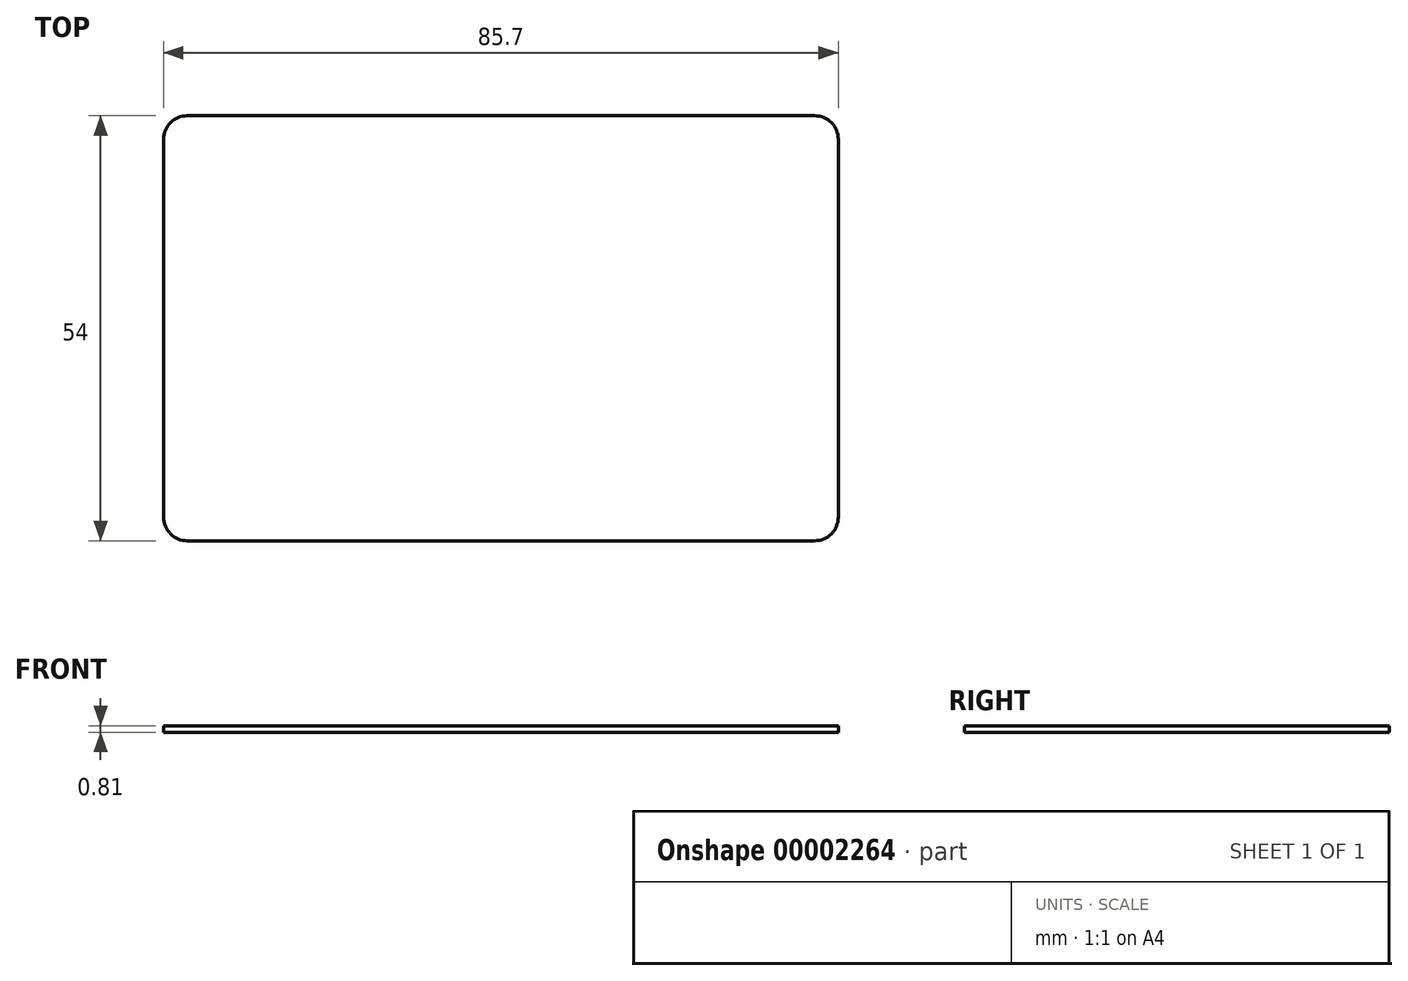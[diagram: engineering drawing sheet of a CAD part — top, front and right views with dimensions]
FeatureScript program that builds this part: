
annotation { "Feature Type Name" : "Feature", "Feature Type Description" : "" }
export const myFeature = defineFeature(function(context is Context, id is Id, definition is map)
    precondition{}
    {
        {
            var Q0;
            Q0=qCreatedBy(makeId("Top.planeOp"),FACE);
            var sketch = newSketch(context, id + "F0", { "sketchPlane" : qUnion([Q0])});
            skLineSegment(sketch, "E0.rect.bottom", {"start": v(39.85, 27) * mm, "end": v(-39.85, 27) * mm});
            skLineSegment(sketch, "E0.rect.top", {"start": v(39.85, -27) * mm, "end": v(-39.85, -27) * mm});
            skLineSegment(sketch, "E0.rect.left", {"start": v(42.85, 24) * mm, "end": v(42.85, -24) * mm});
            skLineSegment(sketch, "E0.rect.right", {"start": v(-42.85, 24) * mm, "end": v(-42.85, -24) * mm});
            skPoint(sketch, "E0.rect.middle", {"position": v(0, 0) * mm});
            skPoint(sketch, "E1.visualSharp", {"position": v(42.85, 27) * mm});
            skArc(sketch, "E1.filletArc", {"start": v(42.85, 24) * mm, "mid": v(41.97, 26.12) * mm, "end": v(39.85, 27) * mm});
            skPoint(sketch, "E2.visualSharp", {"position": v(42.85, -27) * mm});
            skArc(sketch, "E2.filletArc", {"start": v(39.85, -27) * mm, "mid": v(41.97, -26.12) * mm, "end": v(42.85, -24) * mm});
            skPoint(sketch, "E3.visualSharp", {"position": v(-42.85, -27) * mm});
            skArc(sketch, "E3.filletArc", {"start": v(-42.85, -24) * mm, "mid": v(-41.97, -26.12) * mm, "end": v(-39.85, -27) * mm});
            skPoint(sketch, "E4.visualSharp", {"position": v(-42.85, 27) * mm});
            skArc(sketch, "E4.filletArc", {"start": v(-39.85, 27) * mm, "mid": v(-41.97, 26.12) * mm, "end": v(-42.85, 24) * mm});
            skSolve(sketch);
        }
        {
            var Q0;
            Q0=makeQuery(id+"F0.imprint","IMPRINT",FACE,{"disambiguationData":[TD([[makeQuery(id+"F0.imprint","IMPRINT",EDGE,{"derivedFrom":sQuery(id+"F0.wireOp",EDGE,"E0.rect.bottom")}),1.0]])]});
            extrude(context, id + "F1", {"entities" : qUnion([Q0]), "depth" : .81 * mm});
        }
    });
